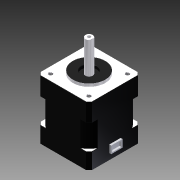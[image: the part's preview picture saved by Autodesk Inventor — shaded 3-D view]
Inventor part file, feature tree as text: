
AUTODESK INVENTOR PART (.ipt)
format: ipt  version: 2012 (Build 160160000, 160)  size: 276,480 bytes
history: native  units: in
note: dims shown in document units (in); Inventor stores cm internally (conversion verified against a paired STEP export)
features: extrude x9, sketch x9, chamfer x4, thread x4
ambient origin geometry x8: Origin, YZ Plane, XZ Plane, XY Plane, X Axis, Y Axis, Z Axis, Center Point
bodies: Solid1 (feature_tree)
feature tree (26):
  extrude  "Extrusion1"  Depth=1.38in
  extrude  "Extrusion2"  Depth=1.655in
  extrude  "Extrusion3"  Depth=0.49in TaperAngle=0.0deg
  chamfer  "Chamfer1"  Distance=0.0787in Angle=45.0deg
  extrude  "Extrusion4"  Depth=0.4in
  extrude  "Extrusion5"  Depth=0.1969in
  extrude  "Extrusion6"  Depth=0.094in
  chamfer  "Chamfer2"  Distance=0.3in
  chamfer  "Chamfer3"  Distance=0.0079in Angle=45.0deg
  extrude  "Extrusion7"  Depth=0.1in TaperAngle=0.0deg
  thread  "Thread4"  [1 undecoded]
  extrude  "Extrusion8"  Depth=0.151in
  extrude  "Extrusion9"  Depth=0.2in
  thread  "Thread5"  [1 undecoded]
  thread  "Thread6"  [1 undecoded]
  thread  "Thread7"  [1 undecoded]
  chamfer  "Chamfer4"  Distance=0.37in
  sketch  "Sketch1"  dims[d0=1.38in d1=1.38in]
  sketch  "Sketch2"  dims[d2=0.434in d3=0.0in d4=1.655in]
  sketch  "Sketch3"  dims[d5=0.657in d6=0.0in d7=0.49in d8=0.0in d9=0.0787in d10=0.125in d11=45.0deg]
  sketch  "Sketch4"  dims[d12=0.864in d13=0.4in]
  sketch  "Sketch5"  dims[d14=0.077in d15=0.0in d16=0.1969in]
  sketch  "Sketch6"  dims[d17=0.85in d18=0.0in d21=0.094in d31=0.3in d32=0.0in d33=0.0079in d34=0.125in d35=45.0deg]
  sketch  "Sketch7"  dims[d36=0.0079in d37=0.125in d38=45.0deg d39=0.1in d40=0.0in d47=1.0in d48=0.0in]
  sketch  "Sketch8"  dims[d49=0.16in d50=0.151in]
  sketch  "Sketch9"  dims[d51=0.151in d52=0.2in d53=0.035in d54=0.035in d55=0.05in d56=0.0in d57=0.37in d58=0.05in d59=0.0in d61=0.7874in d63=1.0236in d64=0.7874in d66=1.0236in d69=0.178in d70=0.1784in d71=0.178in d72=1.0in d73=0.0in d74=1.0in d75=0.0in d76=1.0in d77=0.0in d78=0.01in d79=0.125in d80=45.0deg]
note: 4 required parameter values undecoded (feature->parameter linkage not recoverable at this tier; creation-order binding heuristic only, values carry confidence <= 0.55)
